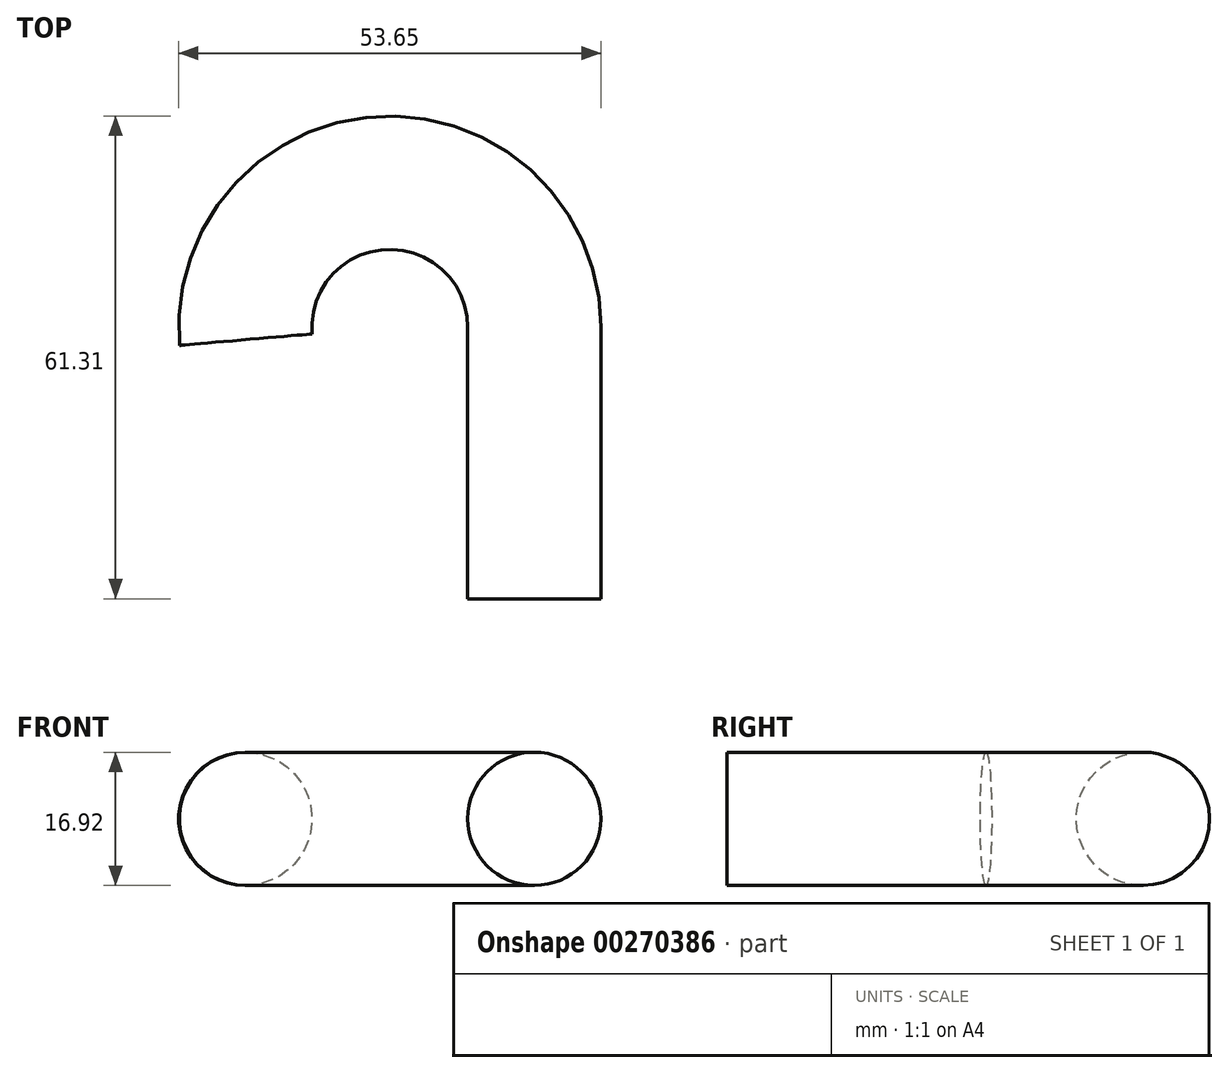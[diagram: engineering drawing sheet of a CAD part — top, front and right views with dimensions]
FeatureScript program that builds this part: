
annotation { "Feature Type Name" : "Feature", "Feature Type Description" : "" }
export const myFeature = defineFeature(function(context is Context, id is Id, definition is map)
    precondition{}
    {
        {
            var Q0;
            Q0=qCreatedBy(makeId("Top.planeOp"),FACE);
            var sketch = newSketch(context, id + "F0", { "sketchPlane" : qUnion([Q0])});
            skLineSegment(sketch, "E0", {"start": v(0, 0) * mm, "end": v(0, 34.49) * mm});
            skArc(sketch, "E1", {"start": v(0, 34.49) * mm, "mid": v(-19.15, 52.83) * mm, "end": v(-36.65, 32.91) * mm});
            skSolve(sketch);
        }
        {
            var Q0;
            Q0=qCreatedBy(makeId("Front.planeOp"),FACE);
            var sketch = newSketch(context, id + "F1", { "sketchPlane" : qUnion([Q0])});
            skCircle(sketch, "E2", {"center": v(0, 0) * mm, "radius": 8.46 * mm});
            skSolve(sketch);
        }
        {
            var Q0;
            Q0=makeQuery(id+"F1.imprint","IMPRINT",FACE,{"disambiguationData":[TD([[makeQuery(id+"F1.imprint","IMPRINT",EDGE,{"derivedFrom":sQuery(id+"F1.wireOp",EDGE,"E2")}),1.0]])]});
            var Q1;
            Q1=sQuery(id+"F0.wireOp",EDGE,"E0");
            var Q2;
            Q2=sQuery(id+"F0.wireOp",EDGE,"E1");
            sweep(context, id + "F2", {"profiles" : qUnion([Q0]), "path" : qUnion([Q1, Q2])});
        }
    });
